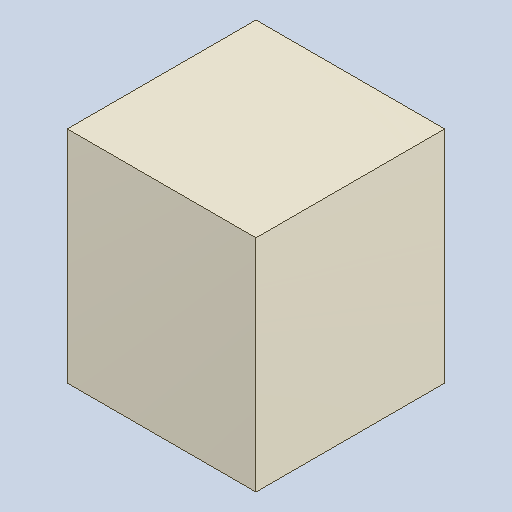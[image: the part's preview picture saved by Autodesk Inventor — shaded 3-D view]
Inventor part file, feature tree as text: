
AUTODESK INVENTOR PART (.ipt)
format: ipt  version: 2023.4 (Build 274418000, 418)  size: 82,944 bytes
history: native  units: mm
features: extrude x1
ambient origin geometry x8: Origin, YZ Plane, XZ Plane, XY Plane, X Axis, Y Axis, Z Axis, Center Point
bodies: Solid1 (feature_tree)
feature tree (1):
  extrude  "Extruded_7"  [1 undecoded]
note: 1 required parameter value undecoded (feature->parameter linkage not recoverable at this tier; creation-order binding heuristic only, values carry confidence <= 0.55)
